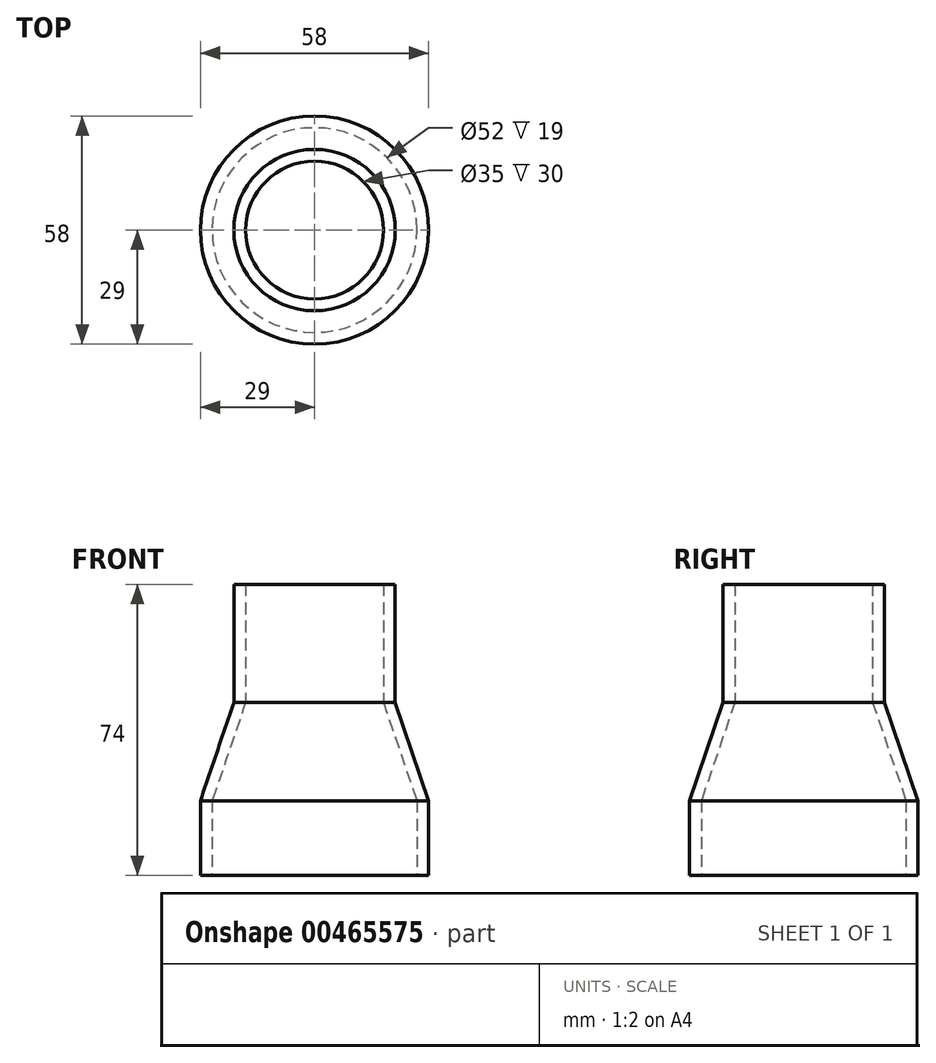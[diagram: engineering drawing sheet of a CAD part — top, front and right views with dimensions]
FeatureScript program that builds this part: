
annotation { "Feature Type Name" : "Feature", "Feature Type Description" : "" }
export const myFeature = defineFeature(function(context is Context, id is Id, definition is map)
    precondition{}
    {
        {
            var Q0;
            Q0=qCreatedBy(makeId("Front.planeOp"),FACE);
            var sketch = newSketch(context, id + "F0", { "sketchPlane" : qUnion([Q0])});
            skLineSegment(sketch, "E0", {"start": v(-20.5, 25) * mm, "end": v(-20.5, 55) * mm});
            skLineSegment(sketch, "E1", {"start": v(-29, -19) * mm, "end": v(-29, 0) * mm});
            skLineSegment(sketch, "E2", {"start": v(-20.5, 25) * mm, "end": v(-29, 0) * mm});
            skLineSegment(sketch, "E3", {"start": v(-20.5, 55) * mm, "end": v(-17.5, 55) * mm});
            skLineSegment(sketch, "E4", {"start": v(-17.5, 55) * mm, "end": v(-17.5, 25) * mm});
            skLineSegment(sketch, "E5", {"start": v(-17.5, 25) * mm, "end": v(-26, 0) * mm});
            skLineSegment(sketch, "E6", {"start": v(-29, -19) * mm, "end": v(-26, -19) * mm});
            skLineSegment(sketch, "E7", {"start": v(-26, -19) * mm, "end": v(-26, 0) * mm});
            skLineSegment(sketch, "E8", {"start": v(0, 0) * mm, "end": v(0, 66.57) * mm, "construction": true});
            skSolve(sketch);
        }
        {
            var Q0;
            Q0=makeQuery(id+"F0.imprint","IMPRINT",FACE,{"disambiguationData":[TD([[makeQuery(id+"F0.imprint","IMPRINT",EDGE,{"derivedFrom":sQuery(id+"F0.wireOp",EDGE,"E0")}),-1.0]])]});
            var Q1;
            Q1=sQuery(id+"F0.wireOp",EDGE,"E8");
            revolve(context, id + "F1", {"surfaceOperationType" : NewSurfaceOperationType.NEW, "entities" : qUnion([Q0]), "axis" : qUnion([Q1]), "revolveType" : RevolveType.FULL});
        }
    });
